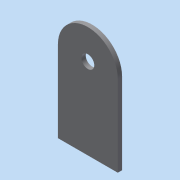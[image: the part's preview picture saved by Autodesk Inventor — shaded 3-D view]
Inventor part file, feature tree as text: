
AUTODESK INVENTOR PART (.ipt)
format: ipt  version: 2013 (Build 170138000, 138)  size: 71,680 bytes
history: native  units: mm
features: other x1, extrude x1, sketch x1
ambient origin geometry x8: Origin, YZ Plane, XZ Plane, XY Plane, X Axis, Y Axis, Z Axis, Center Point
feature tree (3):
  other  "實體1"
  extrude  "擠出1"  Depth=28.0mm
  sketch  "草圖2"
